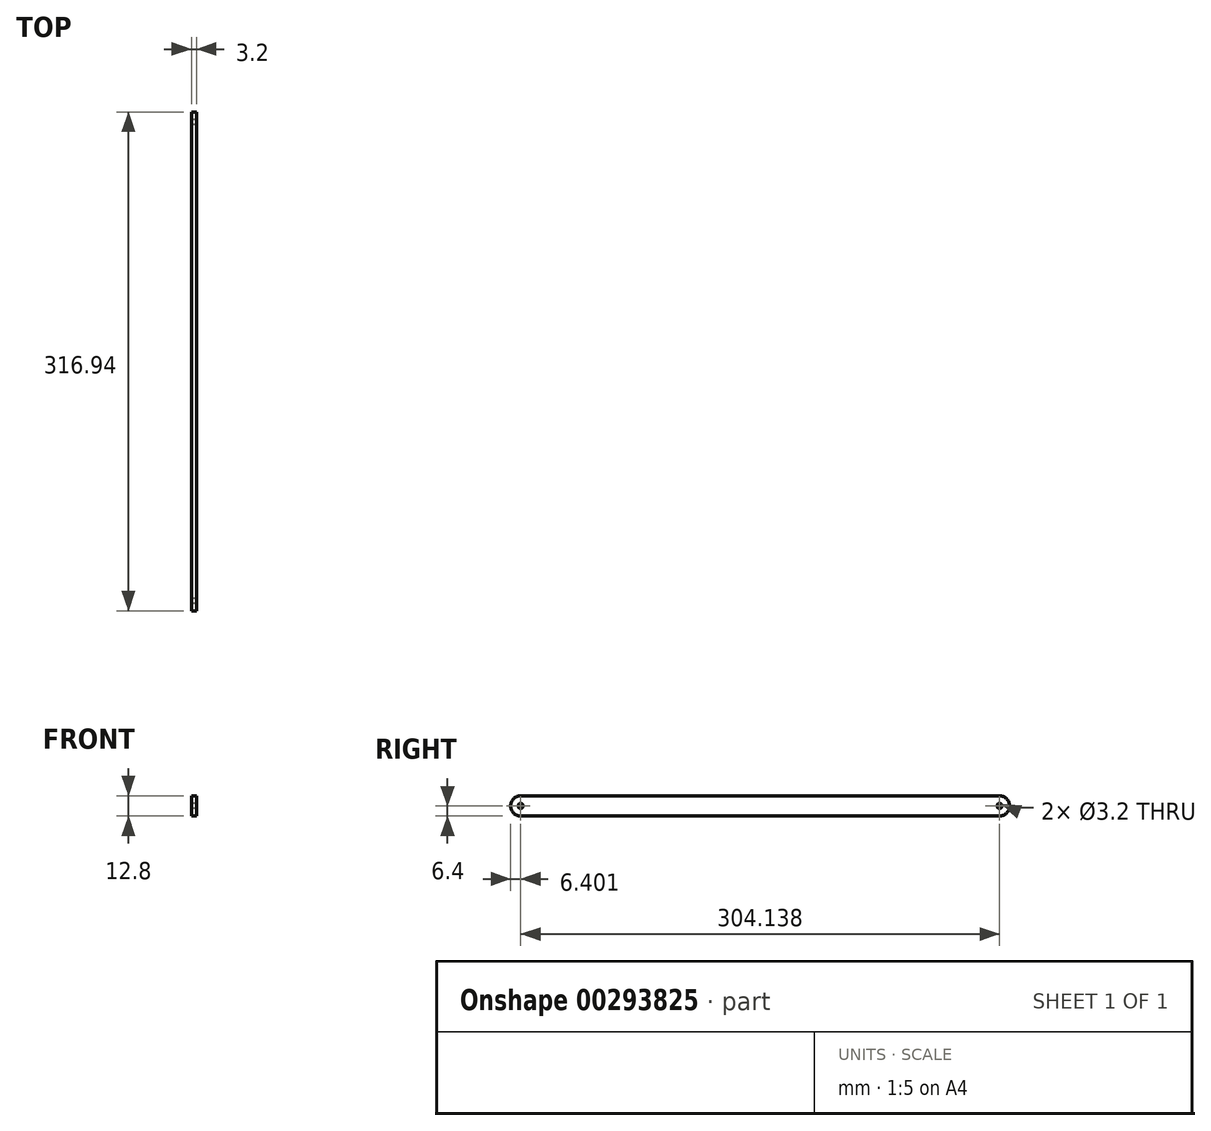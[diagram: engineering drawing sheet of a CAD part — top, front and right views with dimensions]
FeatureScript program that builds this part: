
annotation { "Feature Type Name" : "Feature", "Feature Type Description" : "" }
export const myFeature = defineFeature(function(context is Context, id is Id, definition is map)
    precondition{}
    {
        {
            var Q0;
            Q0=qCreatedBy(makeId("Right.planeOp"),FACE);
            var sketch = newSketch(context, id + "F0", { "sketchPlane" : qUnion([Q0])});
            skLineSegment(sketch, "E0", {"start": v(-152.07, 12.8) * mm, "end": v(152.07, 12.8) * mm});
            skLineSegment(sketch, "E1", {"start": v(-152.07, 0) * mm, "end": v(152.07, 0) * mm});
            skArc(sketch, "E2", {"start": v(-152.07, 12.8) * mm, "mid": v(-158.47, 6.4) * mm, "end": v(-152.07, 0) * mm});
            skArc(sketch, "E3", {"start": v(152.07, 0) * mm, "mid": v(158.47, 6.4) * mm, "end": v(152.07, 12.8) * mm});
            skCircle(sketch, "E4", {"center": v(-152.07, 6.4) * mm, "radius": 1.6 * mm});
            skCircle(sketch, "E5", {"center": v(152.07, 6.4) * mm, "radius": 1.6 * mm});
            skSolve(sketch);
        }
        {
            var Q0;
            Q0 = qSketchRegion(id + "F0", true);
            extrude(context, id + "F1", {"entities" : qUnion([Q0]), "endBound" : BoundingType.SYMMETRIC, "depth" : 3.2 * mm});
        }
    });
